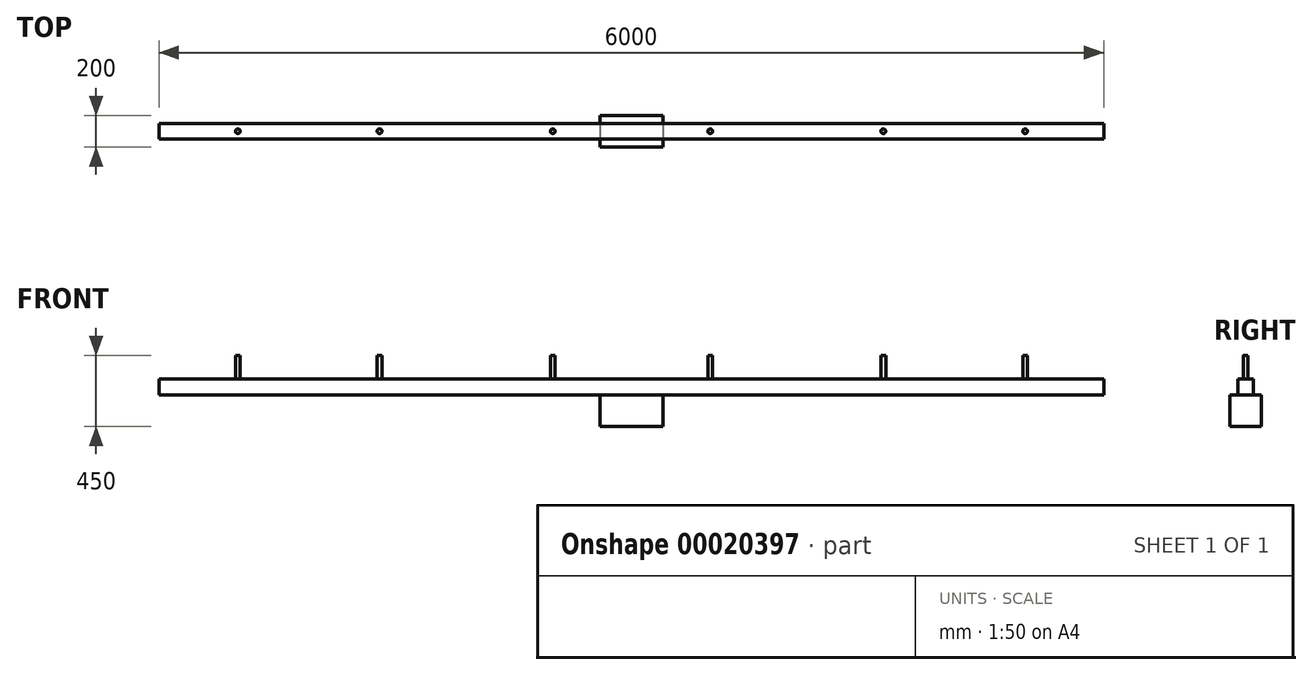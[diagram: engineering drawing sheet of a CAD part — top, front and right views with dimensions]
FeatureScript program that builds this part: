
annotation { "Feature Type Name" : "Feature", "Feature Type Description" : "" }
export const myFeature = defineFeature(function(context is Context, id is Id, definition is map)
    precondition{}
    {
        {
            var Q0;
            Q0=qCreatedBy(makeId("Right.planeOp"),FACE);
            var sketch = newSketch(context, id + "F0", { "sketchPlane" : qUnion([Q0])});
            skLineSegment(sketch, "E0.bottom", {"start": v(0, 0) * mm, "end": v(-100, 0) * mm});
            skLineSegment(sketch, "E0.top", {"start": v(0, 100) * mm, "end": v(-100, 100) * mm});
            skLineSegment(sketch, "E0.left", {"start": v(0, 0) * mm, "end": v(0, 100) * mm});
            skLineSegment(sketch, "E0.right", {"start": v(-100, 0) * mm, "end": v(-100, 100) * mm});
            skSolve(sketch);
        }
        {
            var Q0;
            Q0=makeQuery(id+"F0.imprint","IMPRINT",FACE,{"disambiguationData":[TD([[makeQuery(id+"F0.imprint","IMPRINT",EDGE,{"derivedFrom":sQuery(id+"F0.wireOp",EDGE,"E0.bottom")}),-1.0]])]});
            extrude(context, id + "F1", {"entities" : qUnion([Q0]), "endBound" : BoundingType.SYMMETRIC, "depth" : 6000 * mm});
        }
        {
            var Q0;
            Q0=qCreatedBy(makeId("Top.planeOp"),FACE);
            var sketch = newSketch(context, id + "F2", { "sketchPlane" : qUnion([Q0])});
            skPoint(sketch, "E1.rect.middle", {"position": v(0, 0) * mm});
            skLineSegment(sketch, "E2.bottom", {"start": v(-200, 50) * mm, "end": v(200, 50) * mm});
            skLineSegment(sketch, "E2.top", {"start": v(-200, -150) * mm, "end": v(200, -150) * mm});
            skLineSegment(sketch, "E2.left", {"start": v(-200, 50) * mm, "end": v(-200, -150) * mm});
            skLineSegment(sketch, "E2.right", {"start": v(200, 50) * mm, "end": v(200, -150) * mm});
            skLineSegment(sketch, "E3", {"start": v(0, -199.2) * mm, "end": v(0, 199.2) * mm, "construction": true});
            skSolve(sketch);
        }
        {
            var Q0;
            Q0=makeQuery(id+"F2.imprint","IMPRINT",FACE,{"disambiguationData":[TD([[makeQuery(id+"F2.imprint","IMPRINT",EDGE,{"derivedFrom":sQuery(id+"F2.wireOp",EDGE,"E2.bottom")}),-1.0]])]});
            var Q1;
            Q1=sQuery(id+"F2.wireOp",EDGE,"E2.left");
            var Q2;
            Q2=sQuery(id+"F2.wireOp",EDGE,"E2.top");
            var Q3;
            Q3=sQuery(id+"F2.wireOp",EDGE,"E2.bottom");
            var Q4;
            Q4=sQuery(id+"F2.wireOp",EDGE,"E2.right");
            extrude(context, id + "F3", {"entities" : qUnion([Q0]), "surfaceEntities" : qUnion([Q1, Q2, Q3, Q4]), "oppositeDirection" : true, "depth" : 200 * mm});
        }
        {
            var Q0;
            Q0=makeQuery(id+"F1.opExtrude","SWEPT_FACE",FACE,{"disambiguationData":[OSD([sQuery(id+"F0.wireOp",EDGE,"E0.top")])]});
            var sketch = newSketch(context, id + "F4", { "sketchPlane" : qUnion([Q0])});
            skCircle(sketch, "E4", {"center": v(-500, -50) * mm, "radius": 15 * mm});
            skCircle(sketch, "E5", {"center": v(-1600, -50) * mm, "radius": 15 * mm});
            skCircle(sketch, "E6", {"center": v(-2500, -50) * mm, "radius": 15 * mm});
            skLineSegment(sketch, "E7", {"start": v(3063.02, -50) * mm, "end": v(-3223.66, -50) * mm, "construction": true});
            skLineSegment(sketch, "E8", {"start": v(0, 411.18) * mm, "end": v(0, -663.38) * mm, "construction": true});
            skCircle(sketch, "E9.MirrorC", {"center": v(500, -50) * mm, "radius": 15 * mm});
            skCircle(sketch, "E10.MirrorC", {"center": v(1600, -50) * mm, "radius": 15 * mm});
            skCircle(sketch, "E11.MirrorC", {"center": v(2500, -50) * mm, "radius": 15 * mm});
            skSolve(sketch);
        }
        {
            var Q0;
            Q0 = qSketchRegion(id + "F4", true);
            extrude(context, id + "F5", {"entities" : qUnion([Q0]), "operationType" : NewBodyOperationType.ADD, "depth" : 150 * mm});
        }
    });
